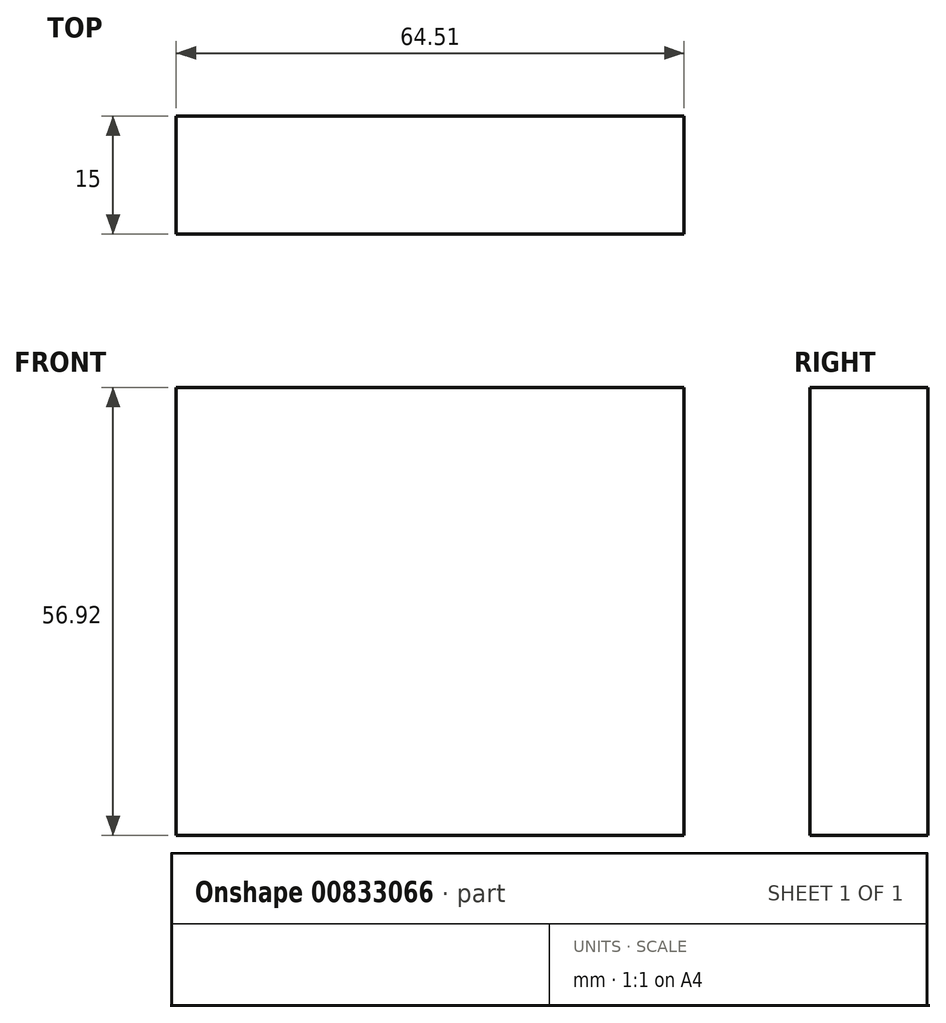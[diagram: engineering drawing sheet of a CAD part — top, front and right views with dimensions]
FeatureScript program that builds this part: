
annotation { "Feature Type Name" : "Feature", "Feature Type Description" : "" }
export const myFeature = defineFeature(function(context is Context, id is Id, definition is map)
    precondition{}
    {
        {
            var Q0;
            Q0=qCreatedBy(makeId("Front.planeOp"),FACE);
            var sketch = newSketch(context, id + "F0", { "sketchPlane" : qUnion([Q0])});
            skLineSegment(sketch, "E0.bottom", {"start": v(-19.92, 32.6) * mm, "end": v(44.6, 32.6) * mm});
            skLineSegment(sketch, "E0.top", {"start": v(-19.92, -24.32) * mm, "end": v(44.6, -24.32) * mm});
            skLineSegment(sketch, "E0.left", {"start": v(-19.92, 32.6) * mm, "end": v(-19.92, -24.32) * mm});
            skLineSegment(sketch, "E0.right", {"start": v(44.6, 32.6) * mm, "end": v(44.6, -24.32) * mm});
            skSolve(sketch);
        }
        {
            var Q0;
            Q0=makeQuery(id+"F0.imprint","IMPRINT",FACE,{"disambiguationData":[TD([[makeQuery(id+"F0.imprint","IMPRINT",EDGE,{"derivedFrom":sQuery(id+"F0.wireOp",EDGE,"E0.bottom")}),-1.0]])]});
            extrude(context, id + "F1", {"entities" : qUnion([Q0]), "depth" : 15 * mm, "offsetDistance" : 25.4 * mm});
        }
    });
